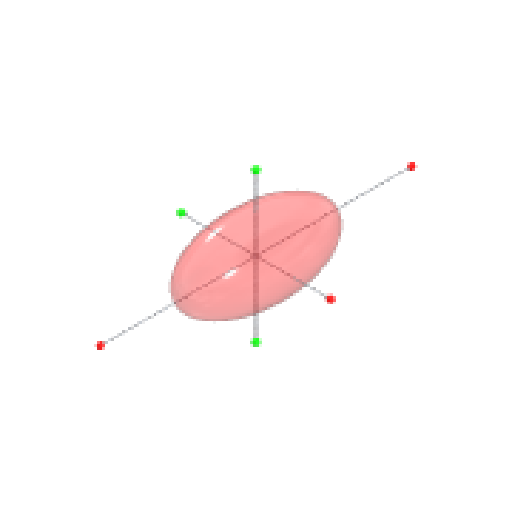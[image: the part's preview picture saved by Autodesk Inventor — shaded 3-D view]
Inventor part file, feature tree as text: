
AUTODESK INVENTOR PART (.ipt)
format: ipt  version: 2023 (Build 270158000, 158)  size: 274,432 bytes
history: native  units: in
note: dims shown in document units (in); Inventor stores cm internally (conversion verified against a paired STEP export)
features: sketch x7, revolve x4, extrude x3, mirror x1, projected_geometry x1
ambient origin geometry x8: Origin, YZ Plane, XZ Plane, XY Plane, X Axis, Y Axis, Z Axis, Center Point
bodies: Solid1 (feature_tree), Solid2 (feature_tree), Solid3 (feature_tree), Solid4 (feature_tree)
feature tree (16):
  revolve  "Revolution1"  [1 undecoded]
  extrude  "Extrusion1"  Depth=1.0in TaperAngle=0.0deg
  mirror  "Mirror1"
  extrude  "Extrusion2"  Depth=1.0in TaperAngle=0.0deg
  extrude  "Extrusion3"  Depth=47.2441in
  revolve  "Revolution2"  [1 undecoded]
  revolve  "Revolution3"  Angle=360.0deg
  revolve  "Revolution4"  [1 undecoded]
  sketch  "Sketch1"  dims[d0=23.622in d1=49.2126in]
  sketch  "Sketch2"  dims[d2=90.0deg d3=1.0in d4=0.0in]
  projected_geometry  "Projected Loop1"
  sketch  "Sketch3"  dims[d5=1.0in d6=0.0in d7=1.0in d8=0.0in]
  sketch  "Sketch4"  dims[d9=47.2441in d10=47.2441in]
  sketch  "Sketch5"  dims[d11=0.25in d12=4.0in]
  sketch  "Sketch6"  dims[d13=4.0in d14=360.0deg]
  sketch  "Sketch7"  dims[d15=98.4252in d16=98.4252in d17=0.25in d18=4.0in d19=4.0in d20=90.0deg d21=47.2441in d22=47.2441in d23=4.0in d24=4.0in d25=0.5in d26=90.0deg d27=0.25in d28=0.25in]
note: 3 required parameter values undecoded (feature->parameter linkage not recoverable at this tier; creation-order binding heuristic only, values carry confidence <= 0.55)
